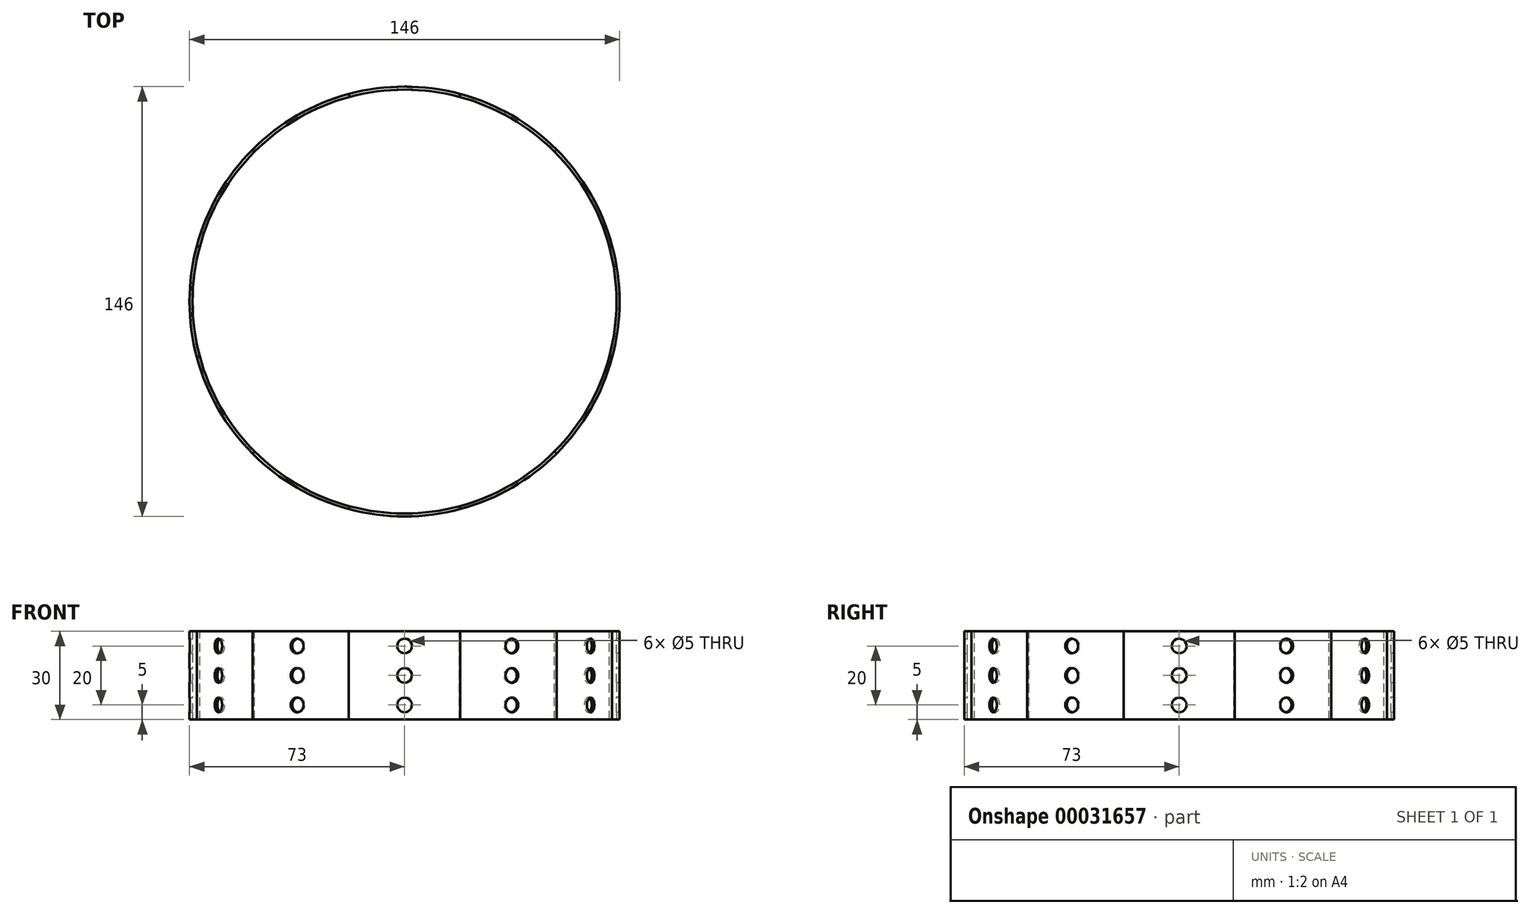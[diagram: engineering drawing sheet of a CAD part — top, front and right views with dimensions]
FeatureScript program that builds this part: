
annotation { "Feature Type Name" : "Feature", "Feature Type Description" : "" }
export const myFeature = defineFeature(function(context is Context, id is Id, definition is map)
    precondition{}
    {
        {
            var Q0;
            Q0=qCreatedBy(makeId("Front.planeOp"),FACE);
            var sketch = newSketch(context, id + "F0", { "sketchPlane" : qUnion([Q0])});
            skLineSegment(sketch, "E0.bottom", {"start": v(-73, 0) * mm, "end": v(-72, 0) * mm});
            skLineSegment(sketch, "E0.top", {"start": v(-73, 30) * mm, "end": v(-72, 30) * mm});
            skLineSegment(sketch, "E0.left", {"start": v(-73, 0) * mm, "end": v(-73, 30) * mm});
            skLineSegment(sketch, "E0.right", {"start": v(-72, 0) * mm, "end": v(-72, 30) * mm});
            skLineSegment(sketch, "E1", {"start": v(0, 0) * mm, "end": v(0, 33.5) * mm, "construction": true});
            skSolve(sketch);
        }
        {
            var Q0;
            Q0=makeQuery(id+"F0.imprint","IMPRINT",FACE,{"disambiguationData":[TD([[makeQuery(id+"F0.imprint","IMPRINT",EDGE,{"derivedFrom":sQuery(id+"F0.wireOp",EDGE,"E0.bottom")}),1.0]])]});
            var Q1;
            Q1=sQuery(id+"F0.wireOp",EDGE,"E1");
            var Q2;
            Q2=sQuery(id+"F0.wireOp",EDGE,"E1");
            revolve(context, id + "F1", {"entities" : qUnion([Q0]), "surfaceEntities" : qUnion([Q1]), "axis" : qUnion([Q2]), "revolveType" : RevolveType.SYMMETRIC, "angle" : 30 * degree});
        }
        {
            var Q0;
            Q0=qCreatedBy(makeId("Right.planeOp"),FACE);
            var sketch = newSketch(context, id + "F2", { "sketchPlane" : qUnion([Q0])});
            skCircle(sketch, "E2", {"center": v(0, 5) * mm, "radius": 2.5 * mm});
            skCircle(sketch, "E3", {"center": v(0, 15) * mm, "radius": 2.5 * mm});
            skCircle(sketch, "E4", {"center": v(0, 25) * mm, "radius": 2.5 * mm});
            skSolve(sketch);
        }
        {
            var Q0;
            Q0 = qSketchRegion(id + "F2", true);
            var Q1;
            Q1=makeQuery(id+"F1.opRevolve","SWEPT_FACE",FACE,{"disambiguationData":[OSD([sQuery(id+"F0.wireOp",EDGE,"E0.left")])]});
            extrude(context, id + "F3", {"entities" : qUnion([Q0]), "operationType" : NewBodyOperationType.REMOVE, "oppositeDirection" : true, "endBoundEntityFace" : qUnion([Q1]), "depth" : 75 * mm});
        }
        {
            var Q0;
            Q0=makeQuery(id+"F1.opRevolve","SWEPT_BODY",BODY,{"disambiguationData":[OSD([sQuery(id+"F0.wireOp",EDGE,"E0.bottom"),sQuery(id+"F0.wireOp",EDGE,"E0.top"),sQuery(id+"F0.wireOp",EDGE,"E0.left"),sQuery(id+"F0.wireOp",EDGE,"E0.right")])]});
            var Q1;
            Q1=sQuery(id+"F0.wireOp",EDGE,"E1");
            circularPattern(context, id + "F4", {"entities" : qUnion([Q0]), "axis" : qUnion([Q1]), "angle" : 360 * degree, "instanceCount" : 12, "equalSpace" : true});
        }
    });
